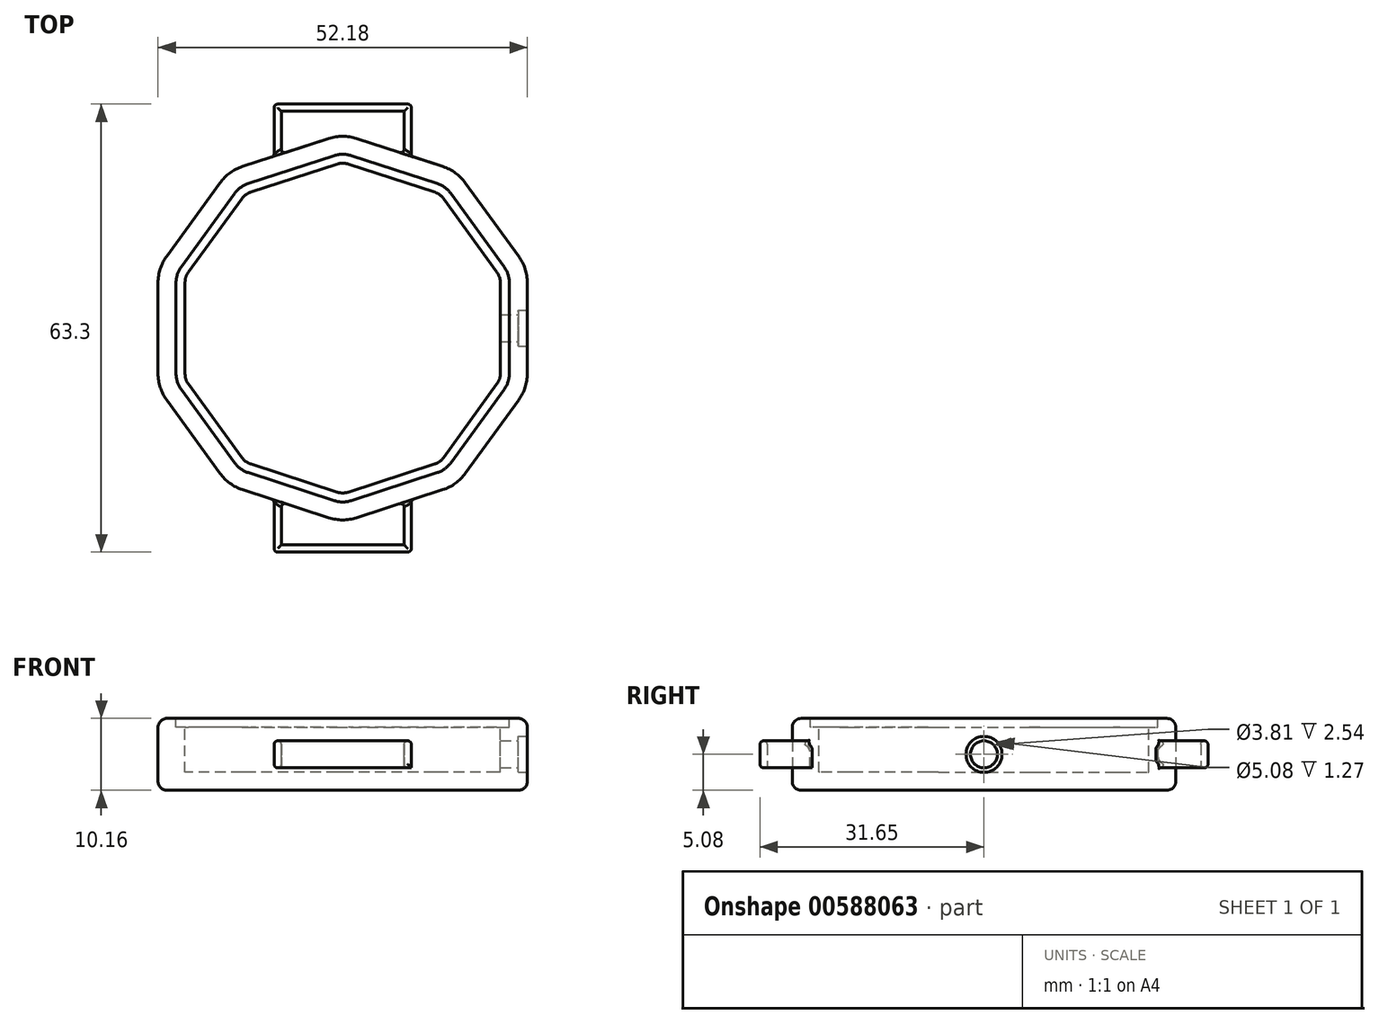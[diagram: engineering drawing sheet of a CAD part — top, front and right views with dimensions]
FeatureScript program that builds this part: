
annotation { "Feature Type Name" : "Feature", "Feature Type Description" : "" }
export const myFeature = defineFeature(function(context is Context, id is Id, definition is map)
    precondition{}
    {
        {
            var Q0;
            Q0=qCreatedBy(makeId("Top.planeOp"),FACE);
            var sketch = newSketch(context, id + "F0", { "sketchPlane" : qUnion([Q0])});
            skCircle(sketch, "E0.cCircle", {"center": v(0, 0) * mm, "radius": 26.09 * mm, "construction": true});
            skLineSegment(sketch, "E0.0", {"start": v(26.09, 8.48) * mm, "end": v(26.09, -8.48) * mm});
            skLineSegment(sketch, "E0.1", {"start": v(26.09, -8.48) * mm, "end": v(16.12, -22.2) * mm});
            skLineSegment(sketch, "E0.2", {"start": v(16.12, -22.2) * mm, "end": v(0, -27.43) * mm});
            skLineSegment(sketch, "E0.3", {"start": v(0, -27.43) * mm, "end": v(-16.12, -22.2) * mm});
            skLineSegment(sketch, "E0.4", {"start": v(-16.12, -22.2) * mm, "end": v(-26.09, -8.48) * mm});
            skLineSegment(sketch, "E0.5", {"start": v(-26.09, -8.48) * mm, "end": v(-26.09, 8.48) * mm});
            skLineSegment(sketch, "E0.6", {"start": v(-26.09, 8.48) * mm, "end": v(-16.12, 22.2) * mm});
            skLineSegment(sketch, "E0.7", {"start": v(-16.12, 22.2) * mm, "end": v(0, 27.43) * mm});
            skLineSegment(sketch, "E0.8", {"start": v(0, 27.43) * mm, "end": v(16.12, 22.2) * mm});
            skLineSegment(sketch, "E0.9", {"start": v(16.12, 22.2) * mm, "end": v(26.09, 8.48) * mm});
            skPoint(sketch, "E0.0.midPoint", {"position": v(26.09, 0) * mm});
            skSolve(sketch);
        }
        {
            var Q0;
            Q0 = qSketchRegion(id + "F0", true);
            extrude(context, id + "F1", {"entities" : qUnion([Q0]), "endBound" : BoundingType.SYMMETRIC, "depth" : 10.16 * mm, "offsetDistance" : 25.4 * mm});
        }
        {
            var Q0;
            Q0=makeQuery(id+"F1.opExtrude","SWEPT_EDGE",EDGE,{"disambiguationData":[OSD([sQuery(id+"F0.wireOp",EDGE,"E0.3"),sQuery(id+"F0.wireOp",EDGE,"E0.4")])]});
            var Q1;
            Q1=makeQuery(id+"F1.opExtrude","SWEPT_EDGE",EDGE,{"disambiguationData":[OSD([sQuery(id+"F0.wireOp",EDGE,"E0.4"),sQuery(id+"F0.wireOp",EDGE,"E0.5")])]});
            var Q2;
            Q2=makeQuery(id+"F1.opExtrude","SWEPT_EDGE",EDGE,{"disambiguationData":[OSD([sQuery(id+"F0.wireOp",EDGE,"E0.5"),sQuery(id+"F0.wireOp",EDGE,"E0.6")])]});
            var Q3;
            Q3=makeQuery(id+"F1.opExtrude","SWEPT_EDGE",EDGE,{"disambiguationData":[OSD([sQuery(id+"F0.wireOp",EDGE,"E0.6"),sQuery(id+"F0.wireOp",EDGE,"E0.7")])]});
            var Q4;
            Q4=makeQuery(id+"F1.opExtrude","SWEPT_EDGE",EDGE,{"disambiguationData":[OSD([sQuery(id+"F0.wireOp",EDGE,"E0.7"),sQuery(id+"F0.wireOp",EDGE,"E0.8")])]});
            var Q5;
            Q5=makeQuery(id+"F1.opExtrude","SWEPT_EDGE",EDGE,{"disambiguationData":[OSD([sQuery(id+"F0.wireOp",EDGE,"E0.8"),sQuery(id+"F0.wireOp",EDGE,"E0.9")])]});
            var Q6;
            Q6=makeQuery(id+"F1.opExtrude","SWEPT_EDGE",EDGE,{"disambiguationData":[OSD([sQuery(id+"F0.wireOp",EDGE,"E0.0"),sQuery(id+"F0.wireOp",EDGE,"E0.9")])]});
            var Q7;
            Q7=makeQuery(id+"F1.opExtrude","SWEPT_EDGE",EDGE,{"disambiguationData":[OSD([sQuery(id+"F0.wireOp",EDGE,"E0.1"),sQuery(id+"F0.wireOp",EDGE,"E0.2")])]});
            var Q8;
            Q8=makeQuery(id+"F1.opExtrude","SWEPT_EDGE",EDGE,{"disambiguationData":[OSD([sQuery(id+"F0.wireOp",EDGE,"E0.2"),sQuery(id+"F0.wireOp",EDGE,"E0.3")])]});
            var Q9;
            Q9=makeQuery(id+"F1.opExtrude","SWEPT_EDGE",EDGE,{"disambiguationData":[OSD([sQuery(id+"F0.wireOp",EDGE,"E0.0"),sQuery(id+"F0.wireOp",EDGE,"E0.1")])]});
            fillet(context, id + "F2", {"entities" : qUnion([Q0, Q1, Q2, Q3, Q4, Q5, Q6, Q7, Q8, Q9]), "radius" : 6.35 * mm, "tangentPropagation" : true, "allowEdgeOverflow" : false});
        }
        {
            var Q0;
            Q0=makeQuery(id+"F1.opExtrude","CAP_FACE",FACE,{"disambiguationData":[OSD([sQuery(id+"F0.wireOp",EDGE,"E0.0"),sQuery(id+"F0.wireOp",EDGE,"E0.1"),sQuery(id+"F0.wireOp",EDGE,"E0.2"),sQuery(id+"F0.wireOp",EDGE,"E0.3"),sQuery(id+"F0.wireOp",EDGE,"E0.4"),sQuery(id+"F0.wireOp",EDGE,"E0.5"),sQuery(id+"F0.wireOp",EDGE,"E0.6"),sQuery(id+"F0.wireOp",EDGE,"E0.7"),sQuery(id+"F0.wireOp",EDGE,"E0.8"),sQuery(id+"F0.wireOp",EDGE,"E0.9")])],"isStart":false});
            fillet(context, id + "F3", {"entities" : qUnion([Q0]), "radius" : 1.27 * mm, "tangentPropagation" : true, "allowEdgeOverflow" : false});
        }
        {
            var Q0;
            Q0=makeQuery(id+"F1.opExtrude","CAP_FACE",FACE,{"disambiguationData":[OSD([sQuery(id+"F0.wireOp",EDGE,"E0.0"),sQuery(id+"F0.wireOp",EDGE,"E0.1"),sQuery(id+"F0.wireOp",EDGE,"E0.2"),sQuery(id+"F0.wireOp",EDGE,"E0.3"),sQuery(id+"F0.wireOp",EDGE,"E0.4"),sQuery(id+"F0.wireOp",EDGE,"E0.5"),sQuery(id+"F0.wireOp",EDGE,"E0.6"),sQuery(id+"F0.wireOp",EDGE,"E0.7"),sQuery(id+"F0.wireOp",EDGE,"E0.8"),sQuery(id+"F0.wireOp",EDGE,"E0.9")])],"isStart":true});
            fillet(context, id + "F4", {"entities" : qUnion([Q0]), "radius" : 1.27 * mm, "tangentPropagation" : true, "allowEdgeOverflow" : false});
        }
        {
            var Q0;
            Q0=makeQuery(id+"F1.opExtrude","CAP_FACE",FACE,{"disambiguationData":[OSD([sQuery(id+"F0.wireOp",EDGE,"E0.0"),sQuery(id+"F0.wireOp",EDGE,"E0.1"),sQuery(id+"F0.wireOp",EDGE,"E0.2"),sQuery(id+"F0.wireOp",EDGE,"E0.3"),sQuery(id+"F0.wireOp",EDGE,"E0.4"),sQuery(id+"F0.wireOp",EDGE,"E0.5"),sQuery(id+"F0.wireOp",EDGE,"E0.6"),sQuery(id+"F0.wireOp",EDGE,"E0.7"),sQuery(id+"F0.wireOp",EDGE,"E0.8"),sQuery(id+"F0.wireOp",EDGE,"E0.9")])],"isStart":false});
            var sketch = newSketch(context, id + "F5", { "sketchPlane" : qUnion([Q0])});
            skLineSegment(sketch, "E1.0", {"start": v(-22.82, -8.65) * mm, "end": v(-15.28, -19.03) * mm});
            skArc(sketch, "E1.1", {"start": v(-23.55, -6.41) * mm, "mid": v(-23.36, -7.6) * mm, "end": v(-22.82, -8.65) * mm});
            skLineSegment(sketch, "E1.2", {"start": v(-23.55, 6.41) * mm, "end": v(-23.55, -6.41) * mm});
            skArc(sketch, "E1.3", {"start": v(-22.82, 8.65) * mm, "mid": v(-23.36, 7.6) * mm, "end": v(-23.55, 6.41) * mm});
            skLineSegment(sketch, "E1.4", {"start": v(-15.28, 19.03) * mm, "end": v(-22.82, 8.65) * mm});
            skArc(sketch, "E1.5", {"start": v(-15.28, -19.03) * mm, "mid": v(-14.44, -19.87) * mm, "end": v(-13.38, -20.41) * mm});
            skArc(sketch, "E1.6", {"start": v(-13.38, 20.41) * mm, "mid": v(-14.44, 19.87) * mm, "end": v(-15.28, 19.03) * mm});
            skLineSegment(sketch, "E1.7", {"start": v(-1.18, 24.38) * mm, "end": v(-13.38, 20.41) * mm});
            skArc(sketch, "E1.8", {"start": v(1.18, 24.38) * mm, "mid": v(0, 24.57) * mm, "end": v(-1.18, 24.38) * mm});
            skLineSegment(sketch, "E1.9", {"start": v(13.38, 20.41) * mm, "end": v(1.18, 24.38) * mm});
            skArc(sketch, "E1.10", {"start": v(13.38, -20.41) * mm, "mid": v(14.44, -19.87) * mm, "end": v(15.28, -19.03) * mm});
            skLineSegment(sketch, "E1.11", {"start": v(1.18, -24.38) * mm, "end": v(13.38, -20.41) * mm});
            skArc(sketch, "E1.12", {"start": v(-1.18, -24.38) * mm, "mid": v(0, -24.57) * mm, "end": v(1.18, -24.38) * mm});
            skLineSegment(sketch, "E1.13", {"start": v(-13.38, -20.41) * mm, "end": v(-1.18, -24.38) * mm});
            skLineSegment(sketch, "E1.14", {"start": v(15.28, -19.03) * mm, "end": v(22.82, -8.65) * mm});
            skArc(sketch, "E1.15", {"start": v(22.82, -8.65) * mm, "mid": v(23.36, -7.6) * mm, "end": v(23.55, -6.41) * mm});
            skLineSegment(sketch, "E1.16", {"start": v(23.55, -6.41) * mm, "end": v(23.55, 6.41) * mm});
            skArc(sketch, "E1.17", {"start": v(23.55, 6.41) * mm, "mid": v(23.36, 7.6) * mm, "end": v(22.82, 8.65) * mm});
            skLineSegment(sketch, "E1.18", {"start": v(22.82, 8.65) * mm, "end": v(15.28, 19.03) * mm});
            skArc(sketch, "E1.19", {"start": v(15.28, 19.03) * mm, "mid": v(14.44, 19.87) * mm, "end": v(13.38, 20.41) * mm});
            skSolve(sketch);
        }
        {
            var Q0;
            Q0=makeQuery(id+"F5.imprint","IMPRINT",FACE,{"disambiguationData":[TD([[makeQuery(id+"F5.imprint","IMPRINT",EDGE,{"derivedFrom":sQuery(id+"F5.wireOp",EDGE,"E1.0")}),1.0]])]});
            var sketch = newSketch(context, id + "F6", { "sketchPlane" : qUnion([Q0])});
            skLineSegment(sketch, "E2.0", {"start": v(14.25, -18.28) * mm, "end": v(21.8, -7.9) * mm});
            skArc(sketch, "E2.1", {"start": v(12.98, -19.2) * mm, "mid": v(13.7, -18.85) * mm, "end": v(14.25, -18.28) * mm});
            skLineSegment(sketch, "E2.2", {"start": v(0.78, -23.17) * mm, "end": v(12.98, -19.2) * mm});
            skArc(sketch, "E2.3", {"start": v(-0.78, -23.17) * mm, "mid": v(0, -23.3) * mm, "end": v(0.78, -23.17) * mm});
            skLineSegment(sketch, "E2.4", {"start": v(-12.98, -19.2) * mm, "end": v(-0.78, -23.17) * mm});
            skArc(sketch, "E2.5", {"start": v(21.8, -7.9) * mm, "mid": v(22.16, -7.2) * mm, "end": v(22.28, -6.41) * mm});
            skArc(sketch, "E2.6", {"start": v(-14.25, -18.28) * mm, "mid": v(-13.7, -18.85) * mm, "end": v(-12.98, -19.2) * mm});
            skLineSegment(sketch, "E2.7", {"start": v(-21.8, -7.9) * mm, "end": v(-14.25, -18.28) * mm});
            skArc(sketch, "E2.8", {"start": v(-22.28, -6.41) * mm, "mid": v(-22.16, -7.2) * mm, "end": v(-21.8, -7.9) * mm});
            skLineSegment(sketch, "E2.9", {"start": v(-22.28, 6.41) * mm, "end": v(-22.28, -6.41) * mm});
            skArc(sketch, "E2.10", {"start": v(14.25, 18.28) * mm, "mid": v(13.7, 18.85) * mm, "end": v(12.98, 19.2) * mm});
            skLineSegment(sketch, "E2.11", {"start": v(21.8, 7.9) * mm, "end": v(14.25, 18.28) * mm});
            skArc(sketch, "E2.12", {"start": v(22.28, 6.41) * mm, "mid": v(22.16, 7.2) * mm, "end": v(21.8, 7.9) * mm});
            skLineSegment(sketch, "E2.13", {"start": v(22.28, -6.41) * mm, "end": v(22.28, 6.41) * mm});
            skLineSegment(sketch, "E2.14", {"start": v(12.98, 19.2) * mm, "end": v(0.78, 23.17) * mm});
            skArc(sketch, "E2.15", {"start": v(0.78, 23.17) * mm, "mid": v(0, 23.3) * mm, "end": v(-0.78, 23.17) * mm});
            skLineSegment(sketch, "E2.16", {"start": v(-0.78, 23.17) * mm, "end": v(-12.98, 19.2) * mm});
            skArc(sketch, "E2.17", {"start": v(-12.98, 19.2) * mm, "mid": v(-13.7, 18.85) * mm, "end": v(-14.25, 18.28) * mm});
            skLineSegment(sketch, "E2.18", {"start": v(-14.25, 18.28) * mm, "end": v(-21.8, 7.9) * mm});
            skArc(sketch, "E2.19", {"start": v(-21.8, 7.9) * mm, "mid": v(-22.16, 7.2) * mm, "end": v(-22.28, 6.41) * mm});
            skSolve(sketch);
        }
        {
            var Q0;
            Q0=makeQuery(id+"F6.imprint","IMPRINT",FACE,{"disambiguationData":[TD([[makeQuery(id+"F6.imprint","IMPRINT",EDGE,{"derivedFrom":sQuery(id+"F6.wireOp",EDGE,"E2.0")}),1.0]])]});
            extrude(context, id + "F7", {"entities" : qUnion([Q0]), "operationType" : NewBodyOperationType.REMOVE, "oppositeDirection" : true, "depth" : 7.62 * mm, "offsetDistance" : 25.4 * mm});
        }
        {
            var Q0;
            Q0=makeQuery(id+"F5.imprint","IMPRINT",FACE,{"disambiguationData":[TD([[makeQuery(id+"F5.imprint","IMPRINT",EDGE,{"derivedFrom":sQuery(id+"F5.wireOp",EDGE,"E1.0")}),1.0]])]});
            extrude(context, id + "F8", {"entities" : qUnion([Q0]), "operationType" : NewBodyOperationType.REMOVE, "oppositeDirection" : true, "depth" : 1.27 * mm, "offsetDistance" : 25.4 * mm});
        }
        {
            var Q0;
            Q0=makeQuery(id+"F1.opExtrude","SWEPT_FACE",FACE,{"disambiguationData":[OSD([sQuery(id+"F0.wireOp",EDGE,"E0.0")])]});
            var sketch = newSketch(context, id + "F9", { "sketchPlane" : qUnion([Q0])});
            skPoint(sketch, "E3", {"position": v(0, 0) * mm});
            skSolve(sketch);
        }
        {
            var Q0;
            Q0=sQuery(id+"F9.wireOp",VERTEX,"E3");
            var Q1;
            Q1=makeQuery(id+"F1.opExtrude","SWEPT_BODY",BODY,{"disambiguationData":[OSD([sQuery(id+"F0.wireOp",EDGE,"E0.0"),sQuery(id+"F0.wireOp",EDGE,"E0.1"),sQuery(id+"F0.wireOp",EDGE,"E0.2"),sQuery(id+"F0.wireOp",EDGE,"E0.3"),sQuery(id+"F0.wireOp",EDGE,"E0.4"),sQuery(id+"F0.wireOp",EDGE,"E0.5"),sQuery(id+"F0.wireOp",EDGE,"E0.6"),sQuery(id+"F0.wireOp",EDGE,"E0.7"),sQuery(id+"F0.wireOp",EDGE,"E0.8"),sQuery(id+"F0.wireOp",EDGE,"E0.9")])]});
            hole(context, id + "F10", {"style" : HoleStyle.C_BORE, "endStyle" : HoleEndStyle.BLIND, "holeDiameter" : 3.8 * mm, "cBoreDiameter" : 5.08 * mm, "cBoreDepth" : 1.27 * mm, "majorDiameter" : 6.35 * mm, "holeDepth" : 12.7 * mm, "isTappedThrough" : true, "tappedDepth" : 12.7 * mm, "tapClearance" : 3, "locations" : qUnion([Q0]), "scope" : qUnion([Q1])});
        }
        {
            var Q0;
            Q0=qCreatedBy(makeId("Top.planeOp"),FACE);
            var sketch = newSketch(context, id + "F11", { "sketchPlane" : qUnion([Q0])});
            skLineSegment(sketch, "E4", {"start": v(-9.7, -23.8) * mm, "end": v(-9.7, -31.65) * mm});
            skLineSegment(sketch, "E5", {"start": v(-9.7, -31.65) * mm, "end": v(0, -31.65) * mm});
            skLineSegment(sketch, "E6.MirrorCS", {"start": v(9.7, -23.8) * mm, "end": v(9.7, -31.65) * mm});
            skLineSegment(sketch, "E7.MirrorCS", {"start": v(9.7, -31.65) * mm, "end": v(0, -31.65) * mm});
            skLineSegment(sketch, "E8.MirrorCS", {"start": v(-9.7, 23.8) * mm, "end": v(-9.7, 31.65) * mm});
            skLineSegment(sketch, "E9.MirrorCS", {"start": v(-9.7, 31.65) * mm, "end": v(0, 31.65) * mm});
            skLineSegment(sketch, "E10.MirrorCS", {"start": v(9.7, 31.65) * mm, "end": v(0, 31.65) * mm});
            skLineSegment(sketch, "E11.MirrorCS", {"start": v(9.7, 23.8) * mm, "end": v(9.7, 31.65) * mm});
            skLineSegment(sketch, "E12.0", {"start": v(8.68, 23.8) * mm, "end": v(8.68, 30.63) * mm});
            skLineSegment(sketch, "E12.1", {"start": v(8.68, 30.63) * mm, "end": v(0, 30.63) * mm});
            skLineSegment(sketch, "E12.2", {"start": v(-8.68, 30.63) * mm, "end": v(0, 30.63) * mm});
            skLineSegment(sketch, "E12.3", {"start": v(-8.68, 23.8) * mm, "end": v(-8.68, 30.63) * mm});
            skLineSegment(sketch, "E13.MirrorCS", {"start": v(8.68, -23.8) * mm, "end": v(8.68, -30.63) * mm});
            skLineSegment(sketch, "E14.MirrorCS", {"start": v(8.68, -30.63) * mm, "end": v(0, -30.63) * mm});
            skLineSegment(sketch, "E15.MirrorCS", {"start": v(-8.68, -30.63) * mm, "end": v(0, -30.63) * mm});
            skLineSegment(sketch, "E16.MirrorCS", {"start": v(-8.68, -23.8) * mm, "end": v(-8.68, -30.63) * mm});
            skLineSegment(sketch, "E17", {"start": v(-9.7, -23.8) * mm, "end": v(-8.68, -23.8) * mm});
            skLineSegment(sketch, "E18", {"start": v(8.68, -23.8) * mm, "end": v(9.7, -23.8) * mm});
            skLineSegment(sketch, "E19", {"start": v(-9.7, 23.8) * mm, "end": v(-8.68, 23.8) * mm});
            skLineSegment(sketch, "E20", {"start": v(8.68, 23.8) * mm, "end": v(9.7, 23.8) * mm});
            skSolve(sketch);
        }
        {
            var Q0;
            Q0=makeQuery(id+"F11.imprint","IMPRINT",FACE,{"disambiguationData":[TD([[makeQuery(id+"F11.imprint","IMPRINT",EDGE,{"derivedFrom":sQuery(id+"F11.wireOp",EDGE,"E4")}),1.0]])]});
            var Q1;
            Q1=makeQuery(id+"F11.imprint","IMPRINT",FACE,{"disambiguationData":[TD([[makeQuery(id+"F11.imprint","IMPRINT",EDGE,{"derivedFrom":sQuery(id+"F11.wireOp",EDGE,"E8.MirrorCS")}),-1.0]])]});
            extrude(context, id + "F12", {"entities" : qUnion([Q0, Q1]), "operationType" : NewBodyOperationType.ADD, "endBound" : BoundingType.SYMMETRIC, "depth" : 3.8 * mm, "offsetDistance" : 25.4 * mm});
        }
        {
            var Q0;
            Q0=makeQuery(id+"F12.opExtrude","CAP_FACE",FACE,{"disambiguationData":[OSD([sQuery(id+"F11.wireOp",EDGE,"E4"),sQuery(id+"F11.wireOp",EDGE,"E5"),sQuery(id+"F11.wireOp",EDGE,"E6.MirrorCS"),sQuery(id+"F11.wireOp",EDGE,"E7.MirrorCS"),sQuery(id+"F11.wireOp",EDGE,"E13.MirrorCS"),sQuery(id+"F11.wireOp",EDGE,"E14.MirrorCS"),sQuery(id+"F11.wireOp",EDGE,"E15.MirrorCS"),sQuery(id+"F11.wireOp",EDGE,"E16.MirrorCS"),sQuery(id+"F11.wireOp",EDGE,"E17"),sQuery(id+"F11.wireOp",EDGE,"E18")])],"isStart":false});
            var Q1;
            Q1=makeQuery(id+"F12.opExtrude","CAP_FACE",FACE,{"disambiguationData":[OSD([sQuery(id+"F11.wireOp",EDGE,"E8.MirrorCS"),sQuery(id+"F11.wireOp",EDGE,"E9.MirrorCS"),sQuery(id+"F11.wireOp",EDGE,"E10.MirrorCS"),sQuery(id+"F11.wireOp",EDGE,"E11.MirrorCS"),sQuery(id+"F11.wireOp",EDGE,"E12.0"),sQuery(id+"F11.wireOp",EDGE,"E12.1"),sQuery(id+"F11.wireOp",EDGE,"E12.2"),sQuery(id+"F11.wireOp",EDGE,"E12.3"),sQuery(id+"F11.wireOp",EDGE,"E19"),sQuery(id+"F11.wireOp",EDGE,"E20")])],"isStart":false});
            var Q2;
            Q2=makeQuery(id+"F12.opExtrude","CAP_EDGE",EDGE,{"disambiguationData":[OSD([sQuery(id+"F11.wireOp",EDGE,"E4")])],"isStart":true});
            var Q3;
            Q3=makeQuery(id+"F12.opExtrude","CAP_FACE",FACE,{"disambiguationData":[OSD([sQuery(id+"F11.wireOp",EDGE,"E8.MirrorCS"),sQuery(id+"F11.wireOp",EDGE,"E9.MirrorCS"),sQuery(id+"F11.wireOp",EDGE,"E10.MirrorCS"),sQuery(id+"F11.wireOp",EDGE,"E11.MirrorCS"),sQuery(id+"F11.wireOp",EDGE,"E12.0"),sQuery(id+"F11.wireOp",EDGE,"E12.1"),sQuery(id+"F11.wireOp",EDGE,"E12.2"),sQuery(id+"F11.wireOp",EDGE,"E12.3"),sQuery(id+"F11.wireOp",EDGE,"E19"),sQuery(id+"F11.wireOp",EDGE,"E20")])],"isStart":true});
            var Q4;
            Q4=makeQuery(id+"F12.opExtrude","SWEPT_EDGE",EDGE,{"disambiguationData":[OSD([sQuery(id+"F11.wireOp",EDGE,"E10.MirrorCS"),sQuery(id+"F11.wireOp",EDGE,"E11.MirrorCS")])]});
            var Q5;
            Q5=makeQuery(id+"F12.opExtrude","SWEPT_EDGE",EDGE,{"disambiguationData":[OSD([sQuery(id+"F11.wireOp",EDGE,"E8.MirrorCS"),sQuery(id+"F11.wireOp",EDGE,"E9.MirrorCS")])]});
            var Q6;
            Q6=makeQuery(id+"F12.opExtrude","SWEPT_EDGE",EDGE,{"disambiguationData":[OSD([sQuery(id+"F11.wireOp",EDGE,"E4"),sQuery(id+"F11.wireOp",EDGE,"E5")])]});
            var Q7;
            Q7=makeQuery(id+"F12.opExtrude","SWEPT_EDGE",EDGE,{"disambiguationData":[OSD([sQuery(id+"F11.wireOp",EDGE,"E6.MirrorCS"),sQuery(id+"F11.wireOp",EDGE,"E7.MirrorCS")])]});
            var Q8;
            Q8=makeQuery(id+"F12.opExtrude","CAP_EDGE",EDGE,{"disambiguationData":[OSD([sQuery(id+"F11.wireOp",EDGE,"E5"),sQuery(id+"F11.wireOp",EDGE,"E7.MirrorCS")])],"isStart":true});
            fillet(context, id + "F13", {"entities" : qUnion([Q0, Q1, Q2, Q3, Q4, Q5, Q6, Q7, Q8]), "radius" : 0.5 * mm, "tangentPropagation" : true, "allowEdgeOverflow" : false});
        }
    });
